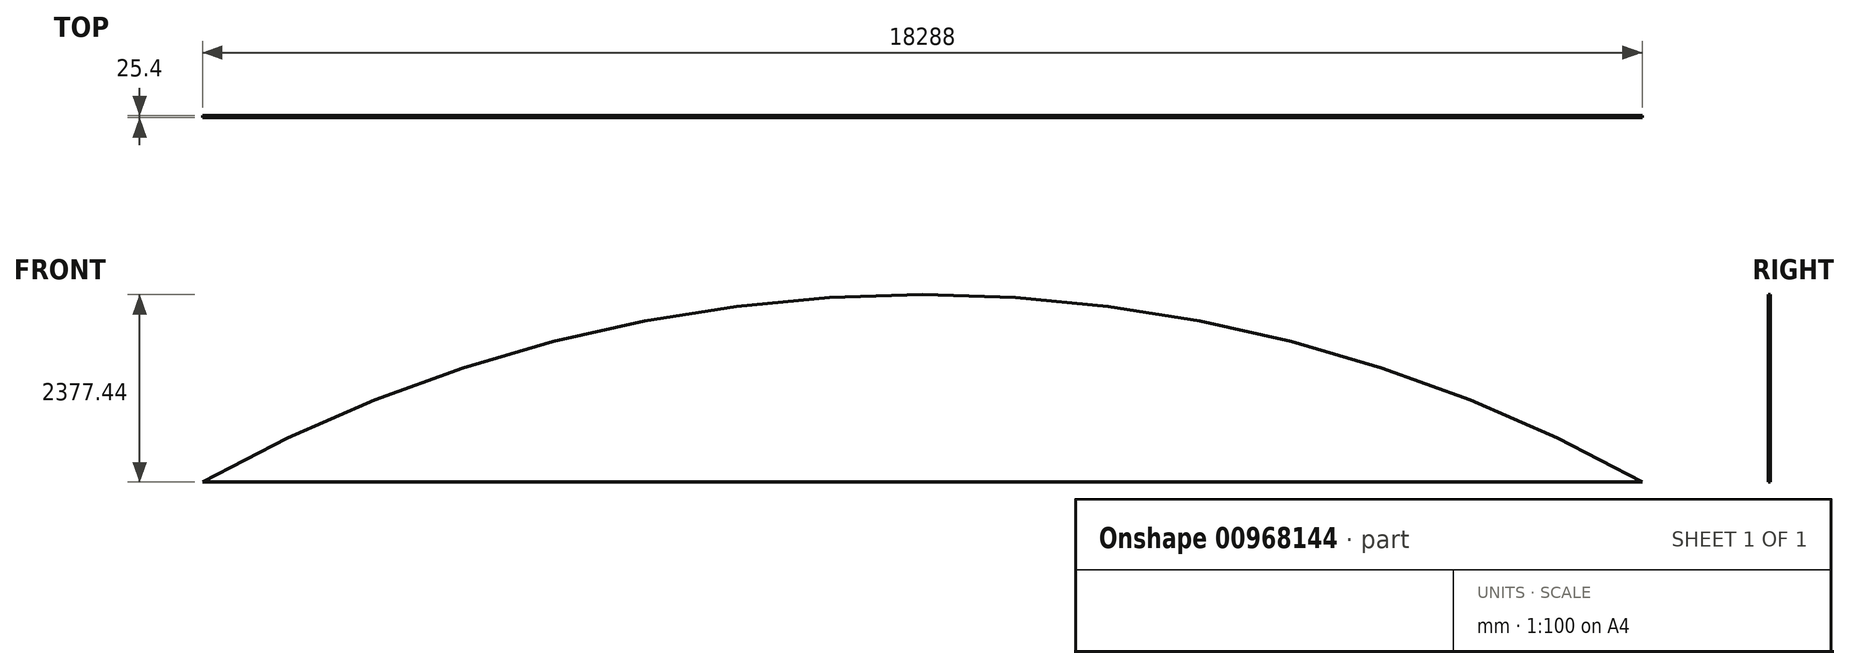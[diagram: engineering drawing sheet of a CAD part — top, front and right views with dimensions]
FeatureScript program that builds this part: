
annotation { "Feature Type Name" : "Feature", "Feature Type Description" : "" }
export const myFeature = defineFeature(function(context is Context, id is Id, definition is map)
    precondition{}
    {
        {
            var Q0;
            Q0=qCreatedBy(makeId("Front.planeOp"),FACE);
            var sketch = newSketch(context, id + "F0", { "sketchPlane" : qUnion([Q0])});
            skLineSegment(sketch, "E0", {"start": v(0, 0) * mm, "end": v(0, 2377.44) * mm, "construction": true});
            skLineSegment(sketch, "E1", {"start": v(0, 0) * mm, "end": v(9144, 0) * mm});
            skLineSegment(sketch, "E2", {"start": v(0, 0) * mm, "end": v(-9144, 0) * mm});
            skArc(sketch, "E3", {"start": v(9144, 0) * mm, "mid": v(0, 2377.44) * mm, "end": v(-9144, 0) * mm});
            skSolve(sketch);
        }
        {
            var Q0;
            Q0=makeQuery(id+"F0.imprint","IMPRINT",FACE,{"disambiguationData":[TD([[makeQuery(id+"F0.imprint","IMPRINT",EDGE,{"derivedFrom":sQuery(id+"F0.wireOp",EDGE,"E1")}),1.0]])]});
            extrude(context, id + "F1", {"entities" : qUnion([Q0]), "depth" : 25.4 * mm, "offsetDistance" : 25.4 * mm});
        }
    });
